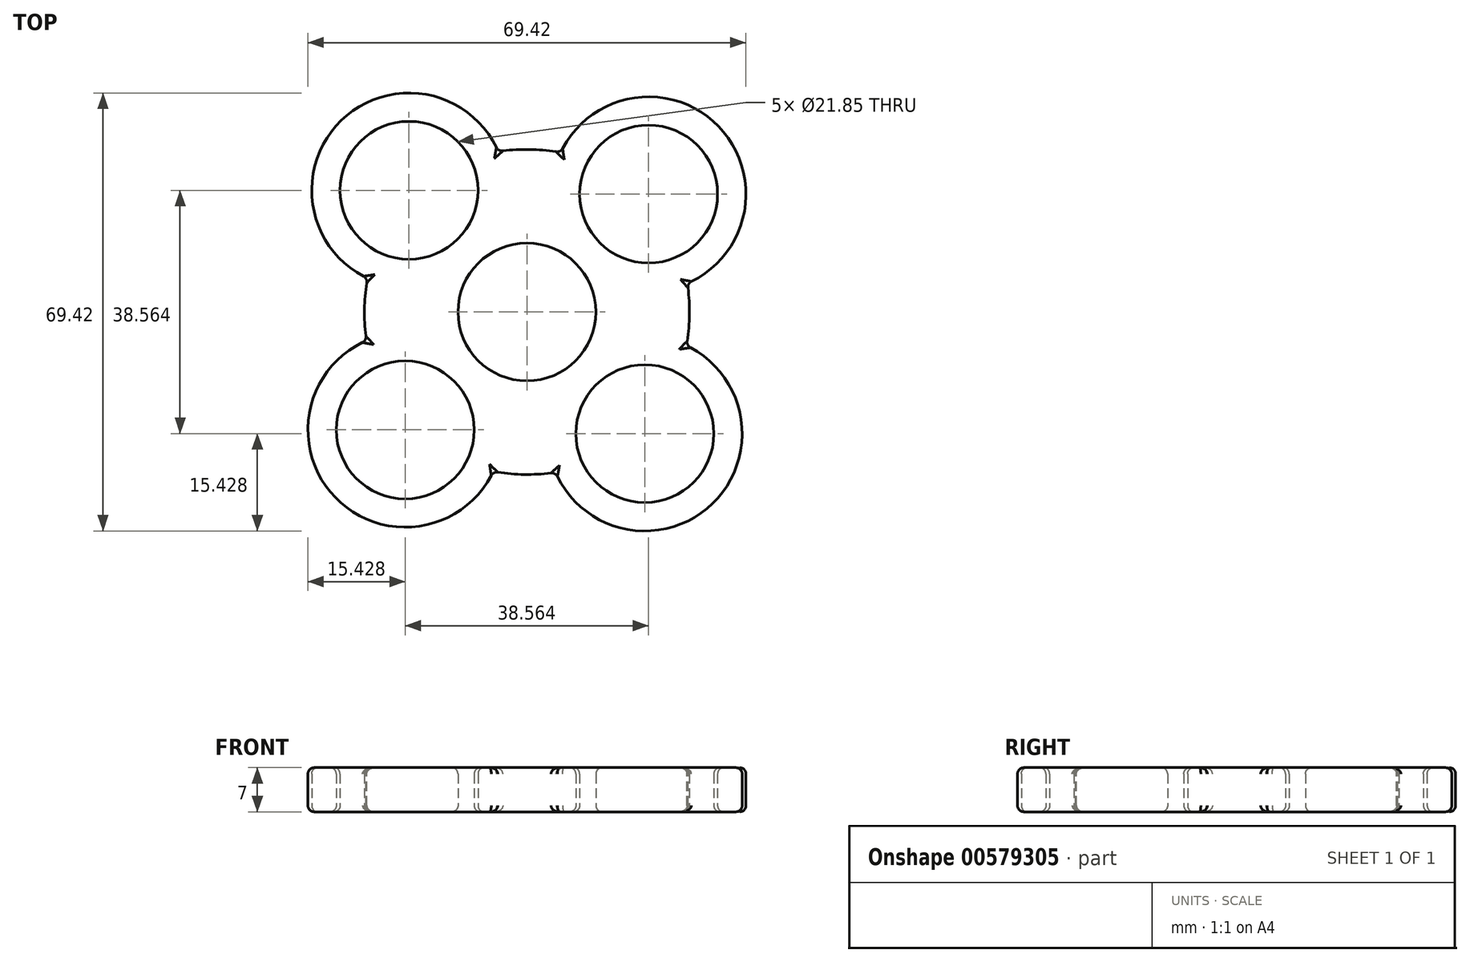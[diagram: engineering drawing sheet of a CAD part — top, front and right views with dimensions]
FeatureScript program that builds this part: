
annotation { "Feature Type Name" : "Feature", "Feature Type Description" : "" }
export const myFeature = defineFeature(function(context is Context, id is Id, definition is map)
    precondition{}
    {
        {
            var Q0;
            Q0=qCreatedBy(makeId("Top.planeOp"),FACE);
            var sketch = newSketch(context, id + "F0", { "sketchPlane" : qUnion([Q0])});
            skCircle(sketch, "E0", {"center": v(0, 0) * mm, "radius": 10.93 * mm});
            skCircle(sketch, "E1", {"center": v(19.28, 18.69) * mm, "radius": 10.93 * mm});
            skPoint(sketch, "E2.orphan", {"position": v(19.28, 0) * mm});
            skPoint(sketch, "E3.end.orphan", {"position": v(0, 20) * mm});
            skPoint(sketch, "E4.orphan", {"position": v(-1.7, 0) * mm});
            skCircle(sketch, "E5.1.0", {"center": v(-18.69, 19.28) * mm, "radius": 10.93 * mm});
            skCircle(sketch, "E5.2.0", {"center": v(-19.28, -18.69) * mm, "radius": 10.93 * mm});
            skCircle(sketch, "E5.3.0", {"center": v(18.69, -19.28) * mm, "radius": 10.93 * mm});
            skArc(sketch, "E6", {"start": v(25.42, 4.54) * mm, "mid": v(30.36, 29.42) * mm, "end": v(5.33, 25.27) * mm});
            skArc(sketch, "E7.1.0", {"start": v(-4.54, 25.42) * mm, "mid": v(-29.42, 30.36) * mm, "end": v(-25.27, 5.33) * mm});
            skArc(sketch, "E7.2.0", {"start": v(-25.42, -4.54) * mm, "mid": v(-30.36, -29.42) * mm, "end": v(-5.33, -25.27) * mm});
            skArc(sketch, "E7.3.0", {"start": v(4.54, -25.42) * mm, "mid": v(29.42, -30.36) * mm, "end": v(25.27, -5.33) * mm});
            skArc(sketch, "E8.1.0", {"start": v(-5.33, -25.27) * mm, "mid": v(-0.4, -25.75) * mm, "end": v(4.54, -25.42) * mm});
            skArc(sketch, "E9.trimOffspring", {"start": v(-25.27, 5.33) * mm, "mid": v(-25.75, 0.4) * mm, "end": v(-25.42, -4.54) * mm});
            skArc(sketch, "E10.trimOffspring", {"start": v(5.33, 25.27) * mm, "mid": v(0.4, 25.75) * mm, "end": v(-4.54, 25.42) * mm});
            skArc(sketch, "E11.trimOffspring", {"start": v(25.27, -5.33) * mm, "mid": v(25.75, -0.4) * mm, "end": v(25.42, 4.54) * mm});
            skSolve(sketch);
        }
        {
            var Q0;
            Q0 = qSketchRegion(id + "F0", true);
            extrude(context, id + "F1", {"entities" : qUnion([Q0]), "depth" : 7 * mm, "offsetDistance" : 25 * mm});
        }
        {
            var Q0;
            Q0=makeQuery(id+"F1.opExtrude","CAP_FACE",FACE,{"disambiguationData":[OSD([sQuery(id+"F0.wireOp",EDGE,"E0"),sQuery(id+"F0.wireOp",EDGE,"E1"),sQuery(id+"F0.wireOp",EDGE,"E5.1.0"),sQuery(id+"F0.wireOp",EDGE,"E5.2.0"),sQuery(id+"F0.wireOp",EDGE,"E5.3.0"),sQuery(id+"F0.wireOp",EDGE,"E6"),sQuery(id+"F0.wireOp",EDGE,"E7.1.0"),sQuery(id+"F0.wireOp",EDGE,"E7.2.0"),sQuery(id+"F0.wireOp",EDGE,"E7.3.0"),sQuery(id+"F0.wireOp",EDGE,"E8.1.0"),sQuery(id+"F0.wireOp",EDGE,"E9.trimOffspring"),sQuery(id+"F0.wireOp",EDGE,"E10.trimOffspring"),sQuery(id+"F0.wireOp",EDGE,"E11.trimOffspring")])],"isStart":false});
            var Q1;
            Q1=makeQuery(id+"F1.opExtrude","CAP_EDGE",EDGE,{"disambiguationData":[OSD([sQuery(id+"F0.wireOp",EDGE,"E8.1.0")])],"isStart":true});
            var Q2;
            Q2=makeQuery(id+"F1.opExtrude","CAP_FACE",FACE,{"disambiguationData":[OSD([sQuery(id+"F0.wireOp",EDGE,"E0"),sQuery(id+"F0.wireOp",EDGE,"E1"),sQuery(id+"F0.wireOp",EDGE,"E5.1.0"),sQuery(id+"F0.wireOp",EDGE,"E5.2.0"),sQuery(id+"F0.wireOp",EDGE,"E5.3.0"),sQuery(id+"F0.wireOp",EDGE,"E6"),sQuery(id+"F0.wireOp",EDGE,"E7.1.0"),sQuery(id+"F0.wireOp",EDGE,"E7.2.0"),sQuery(id+"F0.wireOp",EDGE,"E7.3.0"),sQuery(id+"F0.wireOp",EDGE,"E8.1.0"),sQuery(id+"F0.wireOp",EDGE,"E9.trimOffspring"),sQuery(id+"F0.wireOp",EDGE,"E10.trimOffspring"),sQuery(id+"F0.wireOp",EDGE,"E11.trimOffspring")])],"isStart":true});
            fillet(context, id + "F2", {"entities" : qUnion([Q0, Q1, Q2]), "radius" : 1 * mm, "tangentPropagation" : true, "allowEdgeOverflow" : false});
        }
        {
            var Q0;
            Q0=makeQuery(id+"F1.opExtrude","SWEPT_EDGE",EDGE,{"disambiguationData":[OSD([sQuery(id+"F0.wireOp",EDGE,"E7.2.0"),sQuery(id+"F0.wireOp",EDGE,"E9.trimOffspring")])]});
            var Q1;
            Q1=makeQuery(id+"F1.opExtrude","SWEPT_EDGE",EDGE,{"disambiguationData":[OSD([sQuery(id+"F0.wireOp",EDGE,"E7.1.0"),sQuery(id+"F0.wireOp",EDGE,"E9.trimOffspring")])]});
            var Q2;
            Q2=makeQuery(id+"F1.opExtrude","SWEPT_EDGE",EDGE,{"disambiguationData":[OSD([sQuery(id+"F0.wireOp",EDGE,"E7.2.0"),sQuery(id+"F0.wireOp",EDGE,"E8.1.0")])]});
            var Q3;
            Q3=makeQuery(id+"F1.opExtrude","SWEPT_EDGE",EDGE,{"disambiguationData":[OSD([sQuery(id+"F0.wireOp",EDGE,"E7.3.0"),sQuery(id+"F0.wireOp",EDGE,"E8.1.0")])]});
            var Q4;
            Q4=makeQuery(id+"F1.opExtrude","SWEPT_EDGE",EDGE,{"disambiguationData":[OSD([sQuery(id+"F0.wireOp",EDGE,"E6"),sQuery(id+"F0.wireOp",EDGE,"E11.trimOffspring")])]});
            var Q5;
            Q5=makeQuery(id+"F1.opExtrude","SWEPT_EDGE",EDGE,{"disambiguationData":[OSD([sQuery(id+"F0.wireOp",EDGE,"E7.3.0"),sQuery(id+"F0.wireOp",EDGE,"E11.trimOffspring")])]});
            var Q6;
            Q6=makeQuery(id+"F1.opExtrude","SWEPT_EDGE",EDGE,{"disambiguationData":[OSD([sQuery(id+"F0.wireOp",EDGE,"E7.1.0"),sQuery(id+"F0.wireOp",EDGE,"E10.trimOffspring")])]});
            var Q7;
            Q7=makeQuery(id+"F1.opExtrude","SWEPT_EDGE",EDGE,{"disambiguationData":[OSD([sQuery(id+"F0.wireOp",EDGE,"E6"),sQuery(id+"F0.wireOp",EDGE,"E10.trimOffspring")])]});
            fillet(context, id + "F3", {"entities" : qUnion([Q0, Q1, Q2, Q3, Q4, Q5, Q6, Q7]), "radius" : 1 * mm, "tangentPropagation" : true, "allowEdgeOverflow" : false});
        }
    });
